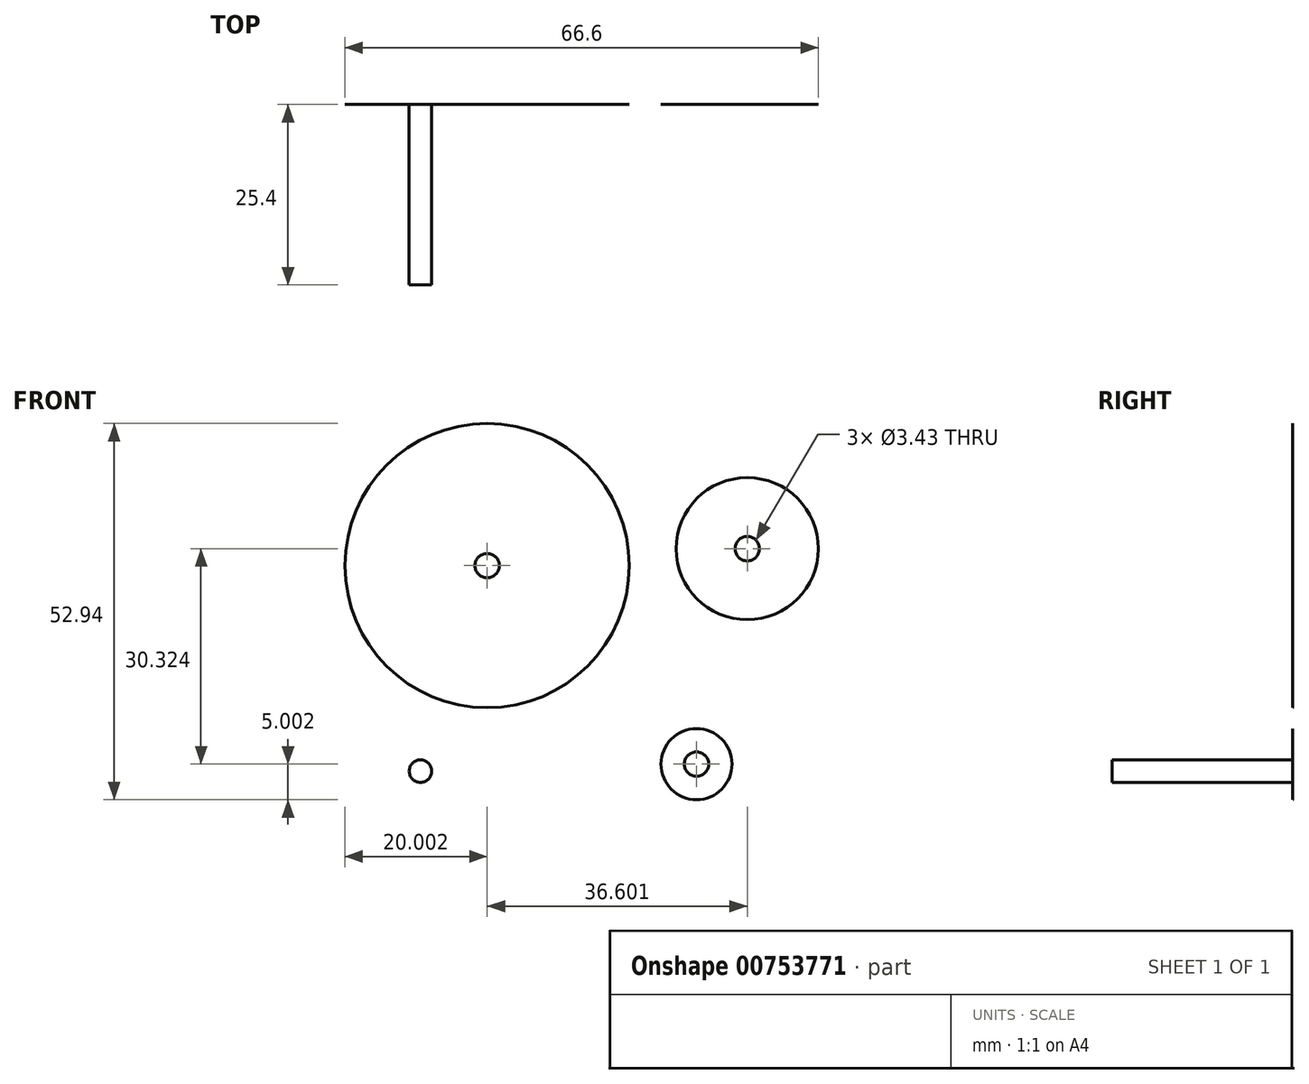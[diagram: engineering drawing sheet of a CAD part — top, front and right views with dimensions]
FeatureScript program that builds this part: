
annotation { "Feature Type Name" : "Feature", "Feature Type Description" : "" }
export const myFeature = defineFeature(function(context is Context, id is Id, definition is map)
    precondition{}
    {
        {
            var Q0;
            Q0=qCreatedBy(makeId("Front.planeOp"),FACE);
            var sketch = newSketch(context, id + "F0", { "sketchPlane" : qUnion([Q0])});
            skCircle(sketch, "E0", {"center": v(-45.29, 43.5) * mm, "radius": 20 * mm});
            skCircle(sketch, "E1", {"center": v(-45.29, 43.5) * mm, "radius": 1.71 * mm});
            skSolve(sketch);
        }
        {
            var Q0;
            Q0 = qSketchRegion(id + "F0", true);
            extrude(context, id + "F1", {"entities" : qUnion([Q0]), "depth" : 1 / 203.2 * mm, "offsetDistance" : 25.4 * mm});
        }
        {
            var Q0;
            Q0=qCreatedBy(makeId("Front.planeOp"),FACE);
            var sketch = newSketch(context, id + "F2", { "sketchPlane" : qUnion([Q0])});
            skCircle(sketch, "E2", {"center": v(-8.69, 45.89) * mm, "radius": 10 * mm});
            skCircle(sketch, "E3", {"center": v(-8.69, 45.89) * mm, "radius": 1.71 * mm});
            skSolve(sketch);
        }
        {
            var Q0;
            Q0 = qSketchRegion(id + "F2", true);
            extrude(context, id + "F3", {"entities" : qUnion([Q0]), "depth" : 1 / 203.2 * mm, "offsetDistance" : 25.4 * mm});
        }
        {
            var Q0;
            Q0=qCreatedBy(makeId("Front.planeOp"),FACE);
            var sketch = newSketch(context, id + "F4", { "sketchPlane" : qUnion([Q0])});
            skCircle(sketch, "E4", {"center": v(-15.83, 15.56) * mm, "radius": 5 * mm});
            skCircle(sketch, "E5", {"center": v(-15.83, 15.56) * mm, "radius": 1.71 * mm});
            skSolve(sketch);
        }
        {
            var Q0;
            Q0 = qSketchRegion(id + "F4", true);
            extrude(context, id + "F5", {"entities" : qUnion([Q0]), "depth" : 1 / 203.2 * mm, "offsetDistance" : 25.4 * mm});
        }
        {
            var Q0;
            Q0=qCreatedBy(makeId("Front.planeOp"),FACE);
            var sketch = newSketch(context, id + "F6", { "sketchPlane" : qUnion([Q0])});
            skCircle(sketch, "E6", {"center": v(-54.66, 14.57) * mm, "radius": 1.59 * mm});
            skSolve(sketch);
        }
        {
            var Q0;
            Q0 = qSketchRegion(id + "F6", true);
            extrude(context, id + "F7", {"entities" : qUnion([Q0]), "depth" : 25.4 * mm, "offsetDistance" : 25.4 * mm});
        }
    });
